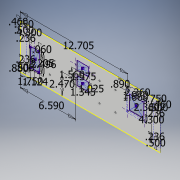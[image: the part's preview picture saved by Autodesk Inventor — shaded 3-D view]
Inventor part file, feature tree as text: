
AUTODESK INVENTOR PART (.ipt)
format: ipt  version: 2017 (Build 210142000, 142)  size: 243,200 bytes
history: native  units: in
note: dims shown in document units (in); Inventor stores cm internally (conversion verified against a paired STEP export)
features: other x5, hole x5, extrude x4, fillet x1, sketch x1
ambient origin geometry x8: Origin, YZ Plane, XZ Plane, XY Plane, X Axis, Y Axis, Z Axis, Center Point
bodies: Solid1 (feature_tree)
feature tree (16):
  extrude  "PDU back"  Depth=5.22in
  other  "pwr entry"
  extrude  "pwr entry cutout"  Depth=0.065in TaperAngle=0.0deg
  hole  "pwr entry holes"  [1 undecoded]
  other  "IEC outlet"
  hole  "IEC holes"  [1 undecoded]
  other  "airflow"
  other  "relay holes"
  hole  "Hole5"  [1 undecoded]
  extrude  "Extrusion6"  Depth=0.196in
  hole  "bracket holes"  [1 undecoded]
  extrude  "Extrusion7"  Depth=0.06in
  fillet  "Fillet3"  [1 undecoded]
  hole  "Hole8"  [1 undecoded]
  sketch  "Sketch1"  dims[d0=16.49in d1=5.22in d2=0.065in d3=0.0in d4=2.205in d5=1.124in d6=2.496in d7=1.75in d8=0.8795in d9=0.06in d10=0.0in d11=0.0in d12=0.136in d13=0.75in d14=0.375in d15=0.25in d16=0.5635in d17=1.0in d18=0.8108in d19=1.025in d20=1.345in d22=1.575in d23=6.59in d24=2.47in d34=0.136in d35=0.75in d36=0.375in d37=0.25in d38=0.5635in d39=1.0in d40=0.8108in d76=2.36in d77=2.36in d78=1.97in d79=1.66in d85=0.177in d86=0.75in d87=0.119in d88=0.25in d89=0.5635in d90=1.0in d91=0.8108in d92=1.0in d93=0.0in d94=0.75in d95=4.3in d96=0.46in d103=0.75in d104=4.3in d105=0.46in d112=0.169in d113=0.75in d114=0.37in d115=0.25in d116=90.0deg d117=1.0in d118=0.8108in d121=0.5in d122=0.236in d123=0.89in d127=0.7874in d129=1.56in d130=0.3937in d132=1.0in d134=1.0in d135=0.0in d136=0.196in d138=1.88in d139=1.46in d143=2.3in d148=1.88in d149=3.76in d150=1.2in d153=12.705in d161=0.5in d162=0.5in d163=0.236in d164=0.236in d165=0.5in d166=0.236in d167=0.177in d168=0.75in d169=0.332in d170=0.25in d171=0.5635in d172=1.0in d173=0.8108in d175=1.2in d176=1.88in d177=1.2in]
  other  "bracket"
note: 6 required parameter values undecoded (feature->parameter linkage not recoverable at this tier; creation-order binding heuristic only, values carry confidence <= 0.55)
